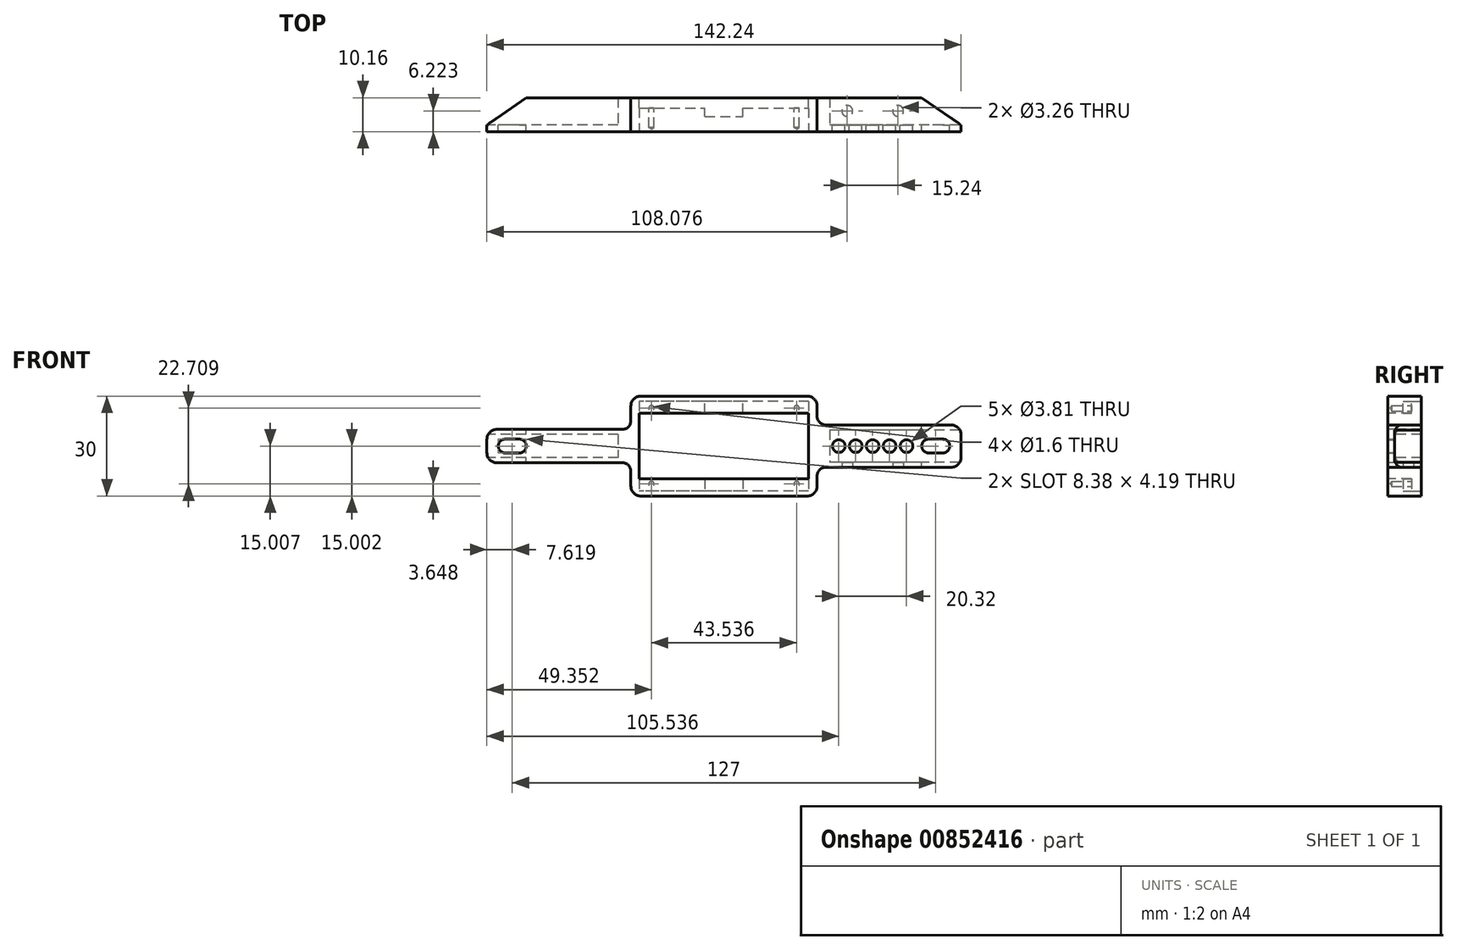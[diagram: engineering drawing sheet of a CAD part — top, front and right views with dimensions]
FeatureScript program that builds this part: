
annotation { "Feature Type Name" : "Feature", "Feature Type Description" : "" }
export const myFeature = defineFeature(function(context is Context, id is Id, definition is map)
    precondition{}
    {
        {
            var Q0;
            Q0=qCreatedBy(makeId("Front.planeOp"),FACE);
            var sketch = newSketch(context, id + "F0", { "sketchPlane" : qUnion([Q0])});
            skLineSegment(sketch, "E0.bottom", {"start": v(21.8, 11.09) * mm, "end": v(72.6, 11.09) * mm});
            skLineSegment(sketch, "E0.top", {"start": v(21.8, -8.62) * mm, "end": v(72.6, -8.62) * mm});
            skLineSegment(sketch, "E0.left", {"start": v(21.8, 11.09) * mm, "end": v(21.8, -8.62) * mm});
            skLineSegment(sketch, "E0.right", {"start": v(72.6, 11.09) * mm, "end": v(72.6, -8.62) * mm});
            skLineSegment(sketch, "E1.bottom", {"start": v(19.27, 16.23) * mm, "end": v(75.15, 16.23) * mm});
            skLineSegment(sketch, "E1.top", {"start": v(19.27, -13.77) * mm, "end": v(75.15, -13.77) * mm});
            skLineSegment(sketch, "E1.left", {"start": v(19.27, 16.23) * mm, "end": v(19.27, -13.77) * mm});
            skLineSegment(sketch, "E1.right", {"start": v(75.15, 16.23) * mm, "end": v(75.15, -13.77) * mm});
            skLineSegment(sketch, "E2.bottom", {"start": v(75.15, 7.58) * mm, "end": v(118.33, 7.58) * mm});
            skLineSegment(sketch, "E2.top", {"start": v(75.15, -5.12) * mm, "end": v(118.33, -5.12) * mm});
            skLineSegment(sketch, "E2.left", {"start": v(75.15, 7.58) * mm, "end": v(75.15, -5.12) * mm});
            skLineSegment(sketch, "E2.right", {"start": v(118.33, 7.58) * mm, "end": v(118.33, -5.12) * mm});
            skLineSegment(sketch, "E3.bottom", {"start": v(19.27, 6.23) * mm, "end": v(-23.91, 6.23) * mm});
            skLineSegment(sketch, "E3.top", {"start": v(19.27, -3.77) * mm, "end": v(-23.91, -3.77) * mm});
            skLineSegment(sketch, "E3.left", {"start": v(19.27, 6.23) * mm, "end": v(19.27, -3.77) * mm});
            skLineSegment(sketch, "E3.right", {"start": v(-23.91, 6.23) * mm, "end": v(-23.91, -3.77) * mm});
            skSolve(sketch);
        }
        {
            var Q0;
            Q0=makeQuery(id+"F0.imprint","IMPRINT",FACE,{"disambiguationData":[TD([[makeQuery(id+"F0.imprint","IMPRINT",EDGE,{"derivedFrom":sQuery(id+"F0.wireOp",EDGE,"E0.bottom")}),1.0]])]});
            var Q1;
            Q1=makeQuery(id+"F0.imprint","IMPRINT",FACE,{"disambiguationData":[TD([[makeQuery(id+"F0.imprint","IMPRINT",EDGE,{"derivedFrom":sQuery(id+"F0.wireOp",EDGE,"E3.bottom")}),1.0]])]});
            var Q2;
            Q2=makeQuery(id+"F0.imprint","IMPRINT",FACE,{"disambiguationData":[TD([[makeQuery(id+"F0.imprint","IMPRINT",EDGE,{"derivedFrom":sQuery(id+"F0.wireOp",EDGE,"E2.bottom")}),-1.0]])]});
            extrude(context, id + "F1", {"entities" : qUnion([Q0, Q1, Q2]), "oppositeDirection" : true, "depth" : 10.16 * mm, "offsetDistance" : 25 * mm});
        }
        {
            var Q0;
            Q0=makeQuery(id+"F1.opExtrude","CAP_FACE",FACE,{"disambiguationData":[OSD([sQuery(id+"F0.wireOp",EDGE,"E0.bottom"),sQuery(id+"F0.wireOp",EDGE,"E0.top"),sQuery(id+"F0.wireOp",EDGE,"E0.left"),sQuery(id+"F0.wireOp",EDGE,"E0.right"),sQuery(id+"F0.wireOp",EDGE,"E1.bottom"),sQuery(id+"F0.wireOp",EDGE,"E1.top"),sQuery(id+"F0.wireOp",EDGE,"E1.left"),sQuery(id+"F0.wireOp",EDGE,"E1.right"),sQuery(id+"F0.wireOp",EDGE,"E2.bottom"),sQuery(id+"F0.wireOp",EDGE,"E2.top"),sQuery(id+"F0.wireOp",EDGE,"E2.right"),sQuery(id+"F0.wireOp",EDGE,"E3.bottom"),sQuery(id+"F0.wireOp",EDGE,"E3.top"),sQuery(id+"F0.wireOp",EDGE,"E3.right")])],"isStart":false});
            var sketch = newSketch(context, id + "F2", { "sketchPlane" : qUnion([Q0])});
            skLineSegment(sketch, "E4.bottom", {"start": v(-72.6, 14.7) * mm, "end": v(-21.8, 14.7) * mm});
            skLineSegment(sketch, "E4.top", {"start": v(-72.6, -12.23) * mm, "end": v(-21.8, -12.23) * mm});
            skLineSegment(sketch, "E4.left", {"start": v(-72.6, 14.7) * mm, "end": v(-72.6, -12.23) * mm});
            skLineSegment(sketch, "E4.right", {"start": v(-21.8, 14.7) * mm, "end": v(-21.8, -12.23) * mm});
            skSolve(sketch);
        }
        {
            var Q0;
            {var subQ0=sQuery(id+"F2.wireOp",EDGE,"E4.top");Q0=makeQuery(id+"F2.imprint","IMPRINT",FACE,{"disambiguationData":[TD([[makeQuery(id+"F2.imprint","IMPRINT",EDGE,{"derivedFrom":subQ0}),1.0]])]});}
            var Q1;
            {var subQ1=makeQuery(id+"F1.opExtrude","CAP_EDGE",EDGE,{"disambiguationData":[OSD([sQuery(id+"F0.wireOp",EDGE,"E0.bottom")])],"isStart":false});Q1=makeQuery(id+"F2.imprint","IMPRINT",FACE,{"disambiguationData":[TD([[makeQuery(id+"F2.imprint","IMPRINT",EDGE,{"derivedFrom":subQ1}),1.0]])]});}
            var Q2;
            {var subQ0=sQuery(id+"F2.wireOp",EDGE,"E4.bottom");Q2=makeQuery(id+"F2.imprint","IMPRINT",FACE,{"disambiguationData":[TD([[makeQuery(id+"F2.imprint","IMPRINT",EDGE,{"derivedFrom":subQ0}),-1.0]])]});}
            extrude(context, id + "F3", {"entities" : qUnion([Q0, Q1, Q2]), "operationType" : NewBodyOperationType.REMOVE, "oppositeDirection" : true, "depth" : 3.05 * mm, "offsetDistance" : 25 * mm});
        }
        {
            var Q0;
            Q0=makeQuery(id+"F1.opExtrude","CAP_FACE",FACE,{"disambiguationData":[OSD([sQuery(id+"F0.wireOp",EDGE,"E0.bottom"),sQuery(id+"F0.wireOp",EDGE,"E0.top"),sQuery(id+"F0.wireOp",EDGE,"E0.left"),sQuery(id+"F0.wireOp",EDGE,"E0.right"),sQuery(id+"F0.wireOp",EDGE,"E1.bottom"),sQuery(id+"F0.wireOp",EDGE,"E1.top"),sQuery(id+"F0.wireOp",EDGE,"E1.left"),sQuery(id+"F0.wireOp",EDGE,"E1.right"),sQuery(id+"F0.wireOp",EDGE,"E2.bottom"),sQuery(id+"F0.wireOp",EDGE,"E2.top"),sQuery(id+"F0.wireOp",EDGE,"E2.right"),sQuery(id+"F0.wireOp",EDGE,"E3.bottom"),sQuery(id+"F0.wireOp",EDGE,"E3.top"),sQuery(id+"F0.wireOp",EDGE,"E3.right")])],"isStart":false});
            var sketch = newSketch(context, id + "F4", { "sketchPlane" : qUnion([Q0])});
            skLineSegment(sketch, "E5.bottom", {"start": v(-118.33, 6.06) * mm, "end": v(-70.07, 6.06) * mm});
            skLineSegment(sketch, "E5.top", {"start": v(-118.33, -3.6) * mm, "end": v(-70.07, -3.6) * mm});
            skLineSegment(sketch, "E5.left", {"start": v(-118.33, 6.06) * mm, "end": v(-118.33, -3.6) * mm});
            skLineSegment(sketch, "E5.right", {"start": v(-70.07, 6.06) * mm, "end": v(-70.07, -3.6) * mm});
            skLineSegment(sketch, "E6.bottom", {"start": v(-24.35, -2.24) * mm, "end": v(36.61, -2.24) * mm});
            skLineSegment(sketch, "E6.top", {"start": v(-24.35, 4.7) * mm, "end": v(36.61, 4.7) * mm});
            skLineSegment(sketch, "E6.left", {"start": v(-24.35, -2.24) * mm, "end": v(-24.35, 4.7) * mm});
            skLineSegment(sketch, "E6.right", {"start": v(36.61, -2.24) * mm, "end": v(36.61, 4.7) * mm});
            skSolve(sketch);
        }
        {
            var Q0;
            Q0=makeQuery(id+"F4.imprint","IMPRINT",FACE,{"disambiguationData":[TD([[makeQuery(id+"F4.imprint","IMPRINT",EDGE,{"derivedFrom":sQuery(id+"F4.wireOp",EDGE,"E5.bottom")}),-1.0]])]});
            var Q1;
            Q1=makeQuery(id+"F4.imprint","IMPRINT",FACE,{"disambiguationData":[TD([[makeQuery(id+"F4.imprint","IMPRINT",EDGE,{"derivedFrom":sQuery(id+"F4.wireOp",EDGE,"E6.bottom")}),1.0]])]});
            extrude(context, id + "F5", {"entities" : qUnion([Q0, Q1]), "operationType" : NewBodyOperationType.REMOVE, "oppositeDirection" : true, "depth" : 8.13 * mm, "offsetDistance" : 25 * mm});
        }
        {
            var Q0;
            Q0=makeQuery(id+"F1.opExtrude","SWEPT_FACE",FACE,{"disambiguationData":[OSD([sQuery(id+"F0.wireOp",EDGE,"E2.bottom")])]});
            var sketch = newSketch(context, id + "F6", { "sketchPlane" : qUnion([Q0])});
            skLineSegment(sketch, "E7", {"start": v(106.52, 10.16) * mm, "end": v(118.33, 2.03) * mm});
            skLineSegment(sketch, "E8", {"start": v(118.33, 2.03) * mm, "end": v(118.33, 0) * mm});
            skLineSegment(sketch, "E9", {"start": v(118.33, 0) * mm, "end": v(106.52, 0) * mm});
            skLineSegment(sketch, "E10", {"start": v(106.52, 0) * mm, "end": v(106.52, 10.16) * mm});
            skSolve(sketch);
        }
        {
            var Q0;
            Q0=makeQuery(id+"F1.opExtrude","SWEPT_FACE",FACE,{"disambiguationData":[OSD([sQuery(id+"F0.wireOp",EDGE,"E3.bottom")])]});
            var sketch = newSketch(context, id + "F7", { "sketchPlane" : qUnion([Q0])});
            skLineSegment(sketch, "E11", {"start": v(-23.91, 2.03) * mm, "end": v(-12.1, 10.16) * mm});
            skLineSegment(sketch, "E12", {"start": v(-12.1, 10.16) * mm, "end": v(-12.1, 0) * mm});
            skLineSegment(sketch, "E13", {"start": v(-12.1, 0) * mm, "end": v(-23.91, 0) * mm});
            skLineSegment(sketch, "E14", {"start": v(-23.91, 0) * mm, "end": v(-23.91, 2.03) * mm});
            skSolve(sketch);
        }
        {
            var Q0;
            {var subQ0=sQuery(id+"F7.wireOp",EDGE,"E11");Q0=makeQuery(id+"F7.imprint","IMPRINT",FACE,{"disambiguationData":[TD([[makeQuery(id+"F7.imprint","IMPRINT",EDGE,{"derivedFrom":subQ0}),1.0]])]});}
            var Q1;
            {var subQ0=sQuery(id+"F6.wireOp",EDGE,"E7");Q1=makeQuery(id+"F6.imprint","IMPRINT",FACE,{"disambiguationData":[TD([[makeQuery(id+"F6.imprint","IMPRINT",EDGE,{"derivedFrom":subQ0}),1.0]])]});}
            extrude(context, id + "F8", {"entities" : qUnion([Q0, Q1]), "operationType" : NewBodyOperationType.REMOVE, "oppositeDirection" : true, "depth" : 25 * mm, "offsetDistance" : 25 * mm});
        }
        {
            var Q0;
            Q0=makeQuery(id+"F5.boolean.opBoolean","COPY",FACE,{"derivedFrom":makeQuery(id+"F5.opExtrude","CAP_FACE",FACE,{"disambiguationData":[OSD([sQuery(id+"F4.wireOp",EDGE,"E5.bottom"),sQuery(id+"F4.wireOp",EDGE,"E5.top"),sQuery(id+"F4.wireOp",EDGE,"E5.left"),sQuery(id+"F4.wireOp",EDGE,"E5.right")])],"isStart":false})});
            var sketch = newSketch(context, id + "F9", { "sketchPlane" : qUnion([Q0])});
            skArc(sketch, "E15", {"start": v(14.2, 3.33) * mm, "mid": v(12.1, 1.24) * mm, "end": v(14.2, -0.86) * mm});
            skArc(sketch, "E16", {"start": v(18.39, -0.86) * mm, "mid": v(20.48, 1.24) * mm, "end": v(18.39, 3.33) * mm});
            skArc(sketch, "E17", {"start": v(-108.61, -0.86) * mm, "mid": v(-106.52, 1.24) * mm, "end": v(-108.61, 3.33) * mm});
            skArc(sketch, "E18", {"start": v(-112.8, 3.33) * mm, "mid": v(-114.9, 1.24) * mm, "end": v(-112.8, -0.86) * mm});
            skLineSegment(sketch, "E19", {"start": v(14.2, 3.33) * mm, "end": v(18.39, 3.33) * mm});
            skLineSegment(sketch, "E20", {"start": v(14.2, -0.86) * mm, "end": v(18.39, -0.86) * mm});
            skLineSegment(sketch, "E21", {"start": v(-112.8, 3.33) * mm, "end": v(-108.61, 3.33) * mm});
            skLineSegment(sketch, "E22", {"start": v(-108.61, -0.86) * mm, "end": v(-112.8, -0.86) * mm});
            skLineSegment(sketch, "E23", {"start": v(18.39, 1.24) * mm, "end": v(14.2, 1.24) * mm});
            skLineSegment(sketch, "E24", {"start": v(-108.61, 1.24) * mm, "end": v(-112.8, 1.24) * mm});
            skPoint(sketch, "E25", {"position": v(-110.7, 1.24) * mm});
            skPoint(sketch, "E26", {"position": v(16.3, 1.24) * mm});
            skLineSegment(sketch, "E27", {"start": v(-72.6, -8.62) * mm, "end": v(-21.8, -8.62) * mm});
            skPoint(sketch, "E28", {"position": v(-47.2, -8.62) * mm});
            skSolve(sketch);
        }
        {
            var Q0;
            Q0=makeQuery(id+"F1.opExtrude","SWEPT_EDGE",EDGE,{"disambiguationData":[OSD([sQuery(id+"F0.wireOp",EDGE,"E1.top"),sQuery(id+"F0.wireOp",EDGE,"E1.right")])]});
            var Q1;
            Q1=makeQuery(id+"F1.opExtrude","SWEPT_EDGE",EDGE,{"disambiguationData":[OSD([sQuery(id+"F0.wireOp",EDGE,"E1.top"),sQuery(id+"F0.wireOp",EDGE,"E1.left")])]});
            var Q2;
            Q2=makeQuery(id+"F1.opExtrude","SWEPT_EDGE",EDGE,{"disambiguationData":[OSD([sQuery(id+"F0.wireOp",EDGE,"E1.bottom"),sQuery(id+"F0.wireOp",EDGE,"E1.left")])]});
            var Q3;
            Q3=makeQuery(id+"F1.opExtrude","SWEPT_EDGE",EDGE,{"disambiguationData":[OSD([sQuery(id+"F0.wireOp",EDGE,"E1.bottom"),sQuery(id+"F0.wireOp",EDGE,"E1.right")])]});
            var Q4;
            Q4=makeQuery(id+"F1.opExtrude","SWEPT_EDGE",EDGE,{"disambiguationData":[OSD([sQuery(id+"F0.wireOp",EDGE,"E3.top"),sQuery(id+"F0.wireOp",EDGE,"E3.right")])]});
            var Q5;
            Q5=makeQuery(id+"F1.opExtrude","SWEPT_EDGE",EDGE,{"disambiguationData":[OSD([sQuery(id+"F0.wireOp",EDGE,"E3.bottom"),sQuery(id+"F0.wireOp",EDGE,"E3.right")])]});
            var Q6;
            Q6=makeQuery(id+"F1.opExtrude","SWEPT_EDGE",EDGE,{"disambiguationData":[OSD([sQuery(id+"F0.wireOp",EDGE,"E2.top"),sQuery(id+"F0.wireOp",EDGE,"E2.right")])]});
            var Q7;
            Q7=makeQuery(id+"F1.opExtrude","SWEPT_EDGE",EDGE,{"disambiguationData":[OSD([sQuery(id+"F0.wireOp",EDGE,"E2.bottom"),sQuery(id+"F0.wireOp",EDGE,"E2.right")])]});
            fillet(context, id + "F10", {"entities" : qUnion([Q0, Q1, Q2, Q3, Q4, Q5, Q6, Q7]), "radius" : 3 * mm, "tangentPropagation" : true, "allowEdgeOverflow" : false});
        }
        {
            var Q0;
            {var subQ0=sQuery(id+"F2.wireOp",EDGE,"E4.top");var subQ1=sQuery(id+"F2.wireOp",EDGE,"E4.left");var subQ2=sQuery(id+"F2.wireOp",EDGE,"E4.right");Q0=makeQuery(id+"F3.boolean.opBoolean","COPY",FACE,{"disambiguationData":[TD([makeQuery(id+"F1.opExtrude","SWEPT_FACE",FACE,{"disambiguationData":[OSD([sQuery(id+"F0.wireOp",EDGE,"E0.top")])]})])],"derivedFrom":makeQuery(id+"F3.opExtrude","CAP_FACE",FACE,{"disambiguationData":[OSD([sQuery(id+"F2.wireOp",EDGE,"E4.bottom"),subQ0,subQ1,subQ2])],"isStart":false})});}
            var sketch = newSketch(context, id + "F11", { "sketchPlane" : qUnion([Q0])});
            skPoint(sketch, "E29", {"position": v(-68.98, 12.59) * mm});
            skPoint(sketch, "E30", {"position": v(-25.44, 12.59) * mm});
            skPoint(sketch, "E31", {"position": v(-25.44, -10.12) * mm});
            skPoint(sketch, "E32", {"position": v(-68.98, -10.12) * mm});
            skSolve(sketch);
        }
        {
            var Q0;
            Q0=sQuery(id+"F11.wireOp",VERTEX,"E29");
            var Q1;
            Q1=sQuery(id+"F11.wireOp",VERTEX,"E30");
            var Q2;
            Q2=sQuery(id+"F11.wireOp",VERTEX,"E31");
            var Q3;
            Q3=sQuery(id+"F11.wireOp",VERTEX,"E32");
            var Q4;
            Q4=makeQuery(id+"F1.opExtrude","SWEPT_BODY",BODY,{"disambiguationData":[OSD([sQuery(id+"F0.wireOp",EDGE,"E0.bottom"),sQuery(id+"F0.wireOp",EDGE,"E0.top"),sQuery(id+"F0.wireOp",EDGE,"E0.left"),sQuery(id+"F0.wireOp",EDGE,"E0.right"),sQuery(id+"F0.wireOp",EDGE,"E1.bottom"),sQuery(id+"F0.wireOp",EDGE,"E1.top"),sQuery(id+"F0.wireOp",EDGE,"E1.left"),sQuery(id+"F0.wireOp",EDGE,"E1.right"),sQuery(id+"F0.wireOp",EDGE,"E2.bottom"),sQuery(id+"F0.wireOp",EDGE,"E2.top"),sQuery(id+"F0.wireOp",EDGE,"E2.right"),sQuery(id+"F0.wireOp",EDGE,"E3.bottom"),sQuery(id+"F0.wireOp",EDGE,"E3.top"),sQuery(id+"F0.wireOp",EDGE,"E3.right")])]});
            hole(context, id + "F12", {"style" : HoleStyle.SIMPLE, "endStyle" : HoleEndStyle.BLIND, "holeDiameter" : 1.6 * mm, "majorDiameter" : 3 * mm, "holeDepth" : 5.84 * mm, "isTappedThrough" : true, "tappedDepth" : 3.18 * mm, "tapClearance" : 3, "startFromSketch" : true, "locations" : qUnion([Q0, Q1, Q2, Q3]), "scope" : qUnion([Q4])});
        }
        {
            var Q0;
            {var subQ0=sQuery(id+"F2.wireOp",EDGE,"E4.bottom");var subQ1=sQuery(id+"F2.wireOp",EDGE,"E4.left");var subQ2=sQuery(id+"F2.wireOp",EDGE,"E4.right");Q0=makeQuery(id+"F3.boolean.opBoolean","COPY",FACE,{"disambiguationData":[TD([makeQuery(id+"F1.opExtrude","SWEPT_FACE",FACE,{"disambiguationData":[OSD([sQuery(id+"F0.wireOp",EDGE,"E0.bottom")])]})])],"derivedFrom":makeQuery(id+"F3.opExtrude","CAP_FACE",FACE,{"disambiguationData":[OSD([subQ0,sQuery(id+"F2.wireOp",EDGE,"E4.top"),subQ1,subQ2])],"isStart":false})});}
            var sketch = newSketch(context, id + "F13", { "sketchPlane" : qUnion([Q0])});
            skLineSegment(sketch, "E33.bottom", {"start": v(-47.2, 11.09) * mm, "end": v(-52.92, 11.09) * mm});
            skLineSegment(sketch, "E33.top", {"start": v(-47.2, 14.7) * mm, "end": v(-52.92, 14.7) * mm});
            skLineSegment(sketch, "E33.left", {"start": v(-47.2, 11.09) * mm, "end": v(-47.2, 14.7) * mm});
            skLineSegment(sketch, "E33.right", {"start": v(-52.92, 11.09) * mm, "end": v(-52.92, 14.7) * mm});
            skLineSegment(sketch, "E34.bottom", {"start": v(-47.2, 11.09) * mm, "end": v(-41.5, 11.09) * mm});
            skLineSegment(sketch, "E34.top", {"start": v(-47.2, 14.7) * mm, "end": v(-41.5, 14.7) * mm});
            skLineSegment(sketch, "E34.right", {"start": v(-41.5, 11.09) * mm, "end": v(-41.5, 14.7) * mm});
            skSolve(sketch);
        }
        {
            var Q0;
            Q0=makeQuery(id+"F13.imprint","IMPRINT",FACE,{"disambiguationData":[TD([[makeQuery(id+"F13.imprint","IMPRINT",EDGE,{"derivedFrom":sQuery(id+"F13.wireOp",EDGE,"E33.bottom")}),-1.0]])]});
            var Q1;
            Q1=makeQuery(id+"F13.imprint","IMPRINT",FACE,{"disambiguationData":[TD([[makeQuery(id+"F13.imprint","IMPRINT",EDGE,{"derivedFrom":sQuery(id+"F13.wireOp",EDGE,"E34.bottom")}),-1.0]])]});
            extrude(context, id + "F14", {"entities" : qUnion([Q0, Q1]), "operationType" : NewBodyOperationType.REMOVE, "oppositeDirection" : true, "depth" : 2.54 * mm, "offsetDistance" : 25.4 * mm});
        }
        {
            var Q0;
            {var subQ0=sQuery(id+"F2.wireOp",EDGE,"E4.top");var subQ1=sQuery(id+"F2.wireOp",EDGE,"E4.left");var subQ2=sQuery(id+"F2.wireOp",EDGE,"E4.right");Q0=makeQuery(id+"F3.boolean.opBoolean","COPY",FACE,{"disambiguationData":[TD([makeQuery(id+"F1.opExtrude","SWEPT_FACE",FACE,{"disambiguationData":[OSD([sQuery(id+"F0.wireOp",EDGE,"E0.top")])]})])],"derivedFrom":makeQuery(id+"F3.opExtrude","CAP_FACE",FACE,{"disambiguationData":[OSD([sQuery(id+"F2.wireOp",EDGE,"E4.bottom"),subQ0,subQ1,subQ2])],"isStart":false})});}
            var sketch = newSketch(context, id + "F15", { "sketchPlane" : qUnion([Q0])});
            skLineSegment(sketch, "E35.bottom", {"start": v(-47.2, -8.62) * mm, "end": v(-52.92, -8.62) * mm});
            skLineSegment(sketch, "E35.top", {"start": v(-47.2, -12.23) * mm, "end": v(-52.92, -12.23) * mm});
            skLineSegment(sketch, "E35.left", {"start": v(-47.2, -8.62) * mm, "end": v(-47.2, -12.23) * mm});
            skLineSegment(sketch, "E35.right", {"start": v(-52.92, -8.62) * mm, "end": v(-52.92, -12.23) * mm});
            skLineSegment(sketch, "E36.bottom", {"start": v(-47.2, -8.62) * mm, "end": v(-41.5, -8.62) * mm});
            skLineSegment(sketch, "E36.top", {"start": v(-47.2, -12.23) * mm, "end": v(-41.5, -12.23) * mm});
            skLineSegment(sketch, "E36.right", {"start": v(-41.5, -8.62) * mm, "end": v(-41.5, -12.23) * mm});
            skSolve(sketch);
        }
        {
            var Q0;
            Q0=makeQuery(id+"F15.imprint","IMPRINT",FACE,{"disambiguationData":[TD([[makeQuery(id+"F15.imprint","IMPRINT",EDGE,{"derivedFrom":sQuery(id+"F15.wireOp",EDGE,"E35.bottom")}),1.0]])]});
            var Q1;
            Q1=makeQuery(id+"F15.imprint","IMPRINT",FACE,{"disambiguationData":[TD([[makeQuery(id+"F15.imprint","IMPRINT",EDGE,{"derivedFrom":sQuery(id+"F15.wireOp",EDGE,"E36.bottom")}),1.0]])]});
            extrude(context, id + "F16", {"entities" : qUnion([Q0, Q1]), "operationType" : NewBodyOperationType.REMOVE, "oppositeDirection" : true, "depth" : 2.54 * mm, "offsetDistance" : 25.4 * mm});
        }
        {
            var Q0;
            Q0=makeQuery(id+"F9.imprint","IMPRINT",FACE,{"disambiguationData":[TD([[makeQuery(id+"F9.imprint","IMPRINT",EDGE,{"derivedFrom":sQuery(id+"F9.wireOp",EDGE,"E17")}),1.0]])]});
            var Q1;
            {var subQ0=sQuery(id+"F9.wireOp",EDGE,"E15");Q1=makeQuery(id+"F9.imprint","IMPRINT",FACE,{"disambiguationData":[TD([[makeQuery(id+"F9.imprint","IMPRINT",EDGE,{"derivedFrom":subQ0}),1.0]])]});}
            extrude(context, id + "F17", {"entities" : qUnion([Q0, Q1]), "operationType" : NewBodyOperationType.REMOVE, "oppositeDirection" : true, "depth" : 25.4 * mm, "offsetDistance" : 25.4 * mm});
        }
        {
            var Q0;
            Q0=makeQuery(id+"F1.opExtrude","SWEPT_EDGE",EDGE,{"disambiguationData":[OSD([sQuery(id+"F0.wireOp",EDGE,"E1.right"),sQuery(id+"F0.wireOp",EDGE,"E2.bottom"),sQuery(id+"F0.wireOp",EDGE,"E2.left")])]});
            var Q1;
            Q1=makeQuery(id+"F1.opExtrude","SWEPT_EDGE",EDGE,{"disambiguationData":[OSD([sQuery(id+"F0.wireOp",EDGE,"E1.right"),sQuery(id+"F0.wireOp",EDGE,"E2.top"),sQuery(id+"F0.wireOp",EDGE,"E2.left")])]});
            var Q2;
            Q2=makeQuery(id+"F1.opExtrude","SWEPT_EDGE",EDGE,{"disambiguationData":[OSD([sQuery(id+"F0.wireOp",EDGE,"E1.left"),sQuery(id+"F0.wireOp",EDGE,"E3.bottom"),sQuery(id+"F0.wireOp",EDGE,"E3.left")])]});
            var Q3;
            Q3=makeQuery(id+"F1.opExtrude","SWEPT_EDGE",EDGE,{"disambiguationData":[OSD([sQuery(id+"F0.wireOp",EDGE,"E1.left"),sQuery(id+"F0.wireOp",EDGE,"E3.top"),sQuery(id+"F0.wireOp",EDGE,"E3.left")])]});
            var Q4;
            Q4=makeQuery(id+"FJ1hREFEKTw6oiv_1.boolean.opBoolean","COPY",EDGE,{"derivedFrom":makeQuery(id+"FJ1hREFEKTw6oiv_1.opExtrude","SWEPT_EDGE",EDGE,{"disambiguationData":[OSD([sQuery(id+"FbFH97T3WgE5ZJY_1.wireOp",EDGE,"Wi6u83F7-kWvT-Vw4W-9EHg-jvR4nR4GsFJO.top"),sQuery(id+"FbFH97T3WgE5ZJY_1.wireOp",EDGE,"Wi6u83F7-kWvT-Vw4W-9EHg-jvR4nR4GsFJO.left")])]})});
            var Q5;
            Q5=makeQuery(id+"FJ1hREFEKTw6oiv_1.boolean.opBoolean","COPY",EDGE,{"derivedFrom":makeQuery(id+"FJ1hREFEKTw6oiv_1.opExtrude","SWEPT_EDGE",EDGE,{"disambiguationData":[OSD([sQuery(id+"FbFH97T3WgE5ZJY_1.wireOp",EDGE,"Wi6u83F7-kWvT-Vw4W-9EHg-jvR4nR4GsFJO.bottom"),sQuery(id+"FbFH97T3WgE5ZJY_1.wireOp",EDGE,"Wi6u83F7-kWvT-Vw4W-9EHg-jvR4nR4GsFJO.left")])]})});
            var Q6;
            Q6=makeQuery(id+"FJ1hREFEKTw6oiv_1.boolean.opBoolean","COPY",EDGE,{"derivedFrom":makeQuery(id+"FJ1hREFEKTw6oiv_1.opExtrude","SWEPT_EDGE",EDGE,{"disambiguationData":[OSD([sQuery(id+"FbFH97T3WgE5ZJY_1.wireOp",EDGE,"Mb6S61IP-998h-fMWc-2Jxv-Ha52hazkjscY.bottom"),sQuery(id+"FbFH97T3WgE5ZJY_1.wireOp",EDGE,"Mb6S61IP-998h-fMWc-2Jxv-Ha52hazkjscY.left")])]})});
            var Q7;
            Q7=makeQuery(id+"FJ1hREFEKTw6oiv_1.boolean.opBoolean","COPY",EDGE,{"derivedFrom":makeQuery(id+"FJ1hREFEKTw6oiv_1.opExtrude","SWEPT_EDGE",EDGE,{"disambiguationData":[OSD([sQuery(id+"FbFH97T3WgE5ZJY_1.wireOp",EDGE,"Mb6S61IP-998h-fMWc-2Jxv-Ha52hazkjscY.top"),sQuery(id+"FbFH97T3WgE5ZJY_1.wireOp",EDGE,"Mb6S61IP-998h-fMWc-2Jxv-Ha52hazkjscY.left")])]})});
            fillet(context, id + "F18", {"entities" : qUnion([Q0, Q1, Q2, Q3, Q4, Q5, Q6, Q7]), "radius" : 2.54 * mm, "tangentPropagation" : true, "allowEdgeOverflow" : false});
        }
        {
            var Q0;
            Q0=makeQuery(id+"F5.boolean.opBoolean","COPY",FACE,{"derivedFrom":makeQuery(id+"F5.opExtrude","CAP_FACE",FACE,{"disambiguationData":[OSD([sQuery(id+"F4.wireOp",EDGE,"E5.bottom"),sQuery(id+"F4.wireOp",EDGE,"E5.top"),sQuery(id+"F4.wireOp",EDGE,"E5.left"),sQuery(id+"F4.wireOp",EDGE,"E5.right")])],"isStart":false})});
            var sketch = newSketch(context, id + "F19", { "sketchPlane" : qUnion([Q0])});
            skPoint(sketch, "E37", {"position": v(-81.63, 1.23) * mm});
            skPoint(sketch, "E38", {"position": v(-86.7, 1.23) * mm});
            skPoint(sketch, "E39", {"position": v(-91.79, 1.23) * mm});
            skPoint(sketch, "E40", {"position": v(-101.95, 1.23) * mm});
            skPoint(sketch, "E41", {"position": v(-96.87, 1.23) * mm});
            skLineSegment(sketch, "E42", {"start": v(-81.63, 1.23) * mm, "end": v(-86.7, 1.23) * mm});
            skPoint(sketch, "E43", {"position": v(-84.17, 1.23) * mm});
            skSolve(sketch);
        }
        {
            var Q0;
            Q0=sQuery(id+"F19.wireOp",VERTEX,"E40");
            var Q1;
            Q1=sQuery(id+"F19.wireOp",VERTEX,"E39");
            var Q2;
            Q2=sQuery(id+"F19.wireOp",VERTEX,"E37");
            var Q3;
            Q3=sQuery(id+"F19.wireOp",VERTEX,"E38");
            var Q4;
            Q4=sQuery(id+"F19.wireOp",VERTEX,"E41");
            var Q5;
            Q5=makeQuery(id+"F1.opExtrude","SWEPT_BODY",BODY,{"disambiguationData":[OSD([sQuery(id+"F0.wireOp",EDGE,"E0.bottom"),sQuery(id+"F0.wireOp",EDGE,"E0.top"),sQuery(id+"F0.wireOp",EDGE,"E0.left"),sQuery(id+"F0.wireOp",EDGE,"E0.right"),sQuery(id+"F0.wireOp",EDGE,"E1.bottom"),sQuery(id+"F0.wireOp",EDGE,"E1.top"),sQuery(id+"F0.wireOp",EDGE,"E1.left"),sQuery(id+"F0.wireOp",EDGE,"E1.right"),sQuery(id+"F0.wireOp",EDGE,"E2.bottom"),sQuery(id+"F0.wireOp",EDGE,"E2.top"),sQuery(id+"F0.wireOp",EDGE,"E2.right"),sQuery(id+"F0.wireOp",EDGE,"E3.bottom"),sQuery(id+"F0.wireOp",EDGE,"E3.top"),sQuery(id+"F0.wireOp",EDGE,"E3.right")])]});
            hole(context, id + "F20", {"style" : HoleStyle.SIMPLE, "endStyle" : HoleEndStyle.THROUGH, "holeDiameter" : 3.8 * mm, "majorDiameter" : 6.35 * mm, "isTappedThrough" : true, "tappedDepth" : 3.17 * mm, "tapClearance" : 3, "startFromSketch" : true, "locations" : qUnion([Q0, Q1, Q2, Q3, Q4]), "scope" : qUnion([Q5])});
        }
        {
            var Q0;
            Q0=makeQuery(id+"F5.boolean.opBoolean","COPY",FACE,{"derivedFrom":makeQuery(id+"F5.opExtrude","CAP_FACE",FACE,{"disambiguationData":[OSD([sQuery(id+"F4.wireOp",EDGE,"E5.bottom"),sQuery(id+"F4.wireOp",EDGE,"E5.top"),sQuery(id+"F4.wireOp",EDGE,"E5.left"),sQuery(id+"F4.wireOp",EDGE,"E5.right")])],"isStart":false})});
            var sketch = newSketch(context, id + "F21", { "sketchPlane" : qUnion([Q0])});
            skLineSegment(sketch, "E44.bottom", {"start": v(-72.6, 6.06) * mm, "end": v(-78.96, 6.06) * mm});
            skLineSegment(sketch, "E44.top", {"start": v(-72.6, -3.6) * mm, "end": v(-78.96, -3.6) * mm});
            skLineSegment(sketch, "E44.left", {"start": v(-72.6, 6.06) * mm, "end": v(-72.6, -3.6) * mm});
            skLineSegment(sketch, "E44.right", {"start": v(-78.96, 6.06) * mm, "end": v(-78.96, -3.6) * mm});
            skSolve(sketch);
        }
        {
            var Q0;
            Q0=makeQuery(id+"F5.boolean.opBoolean","COPY",FACE,{"derivedFrom":makeQuery(id+"F5.opExtrude","CAP_FACE",FACE,{"disambiguationData":[OSD([sQuery(id+"F4.wireOp",EDGE,"E6.bottom"),sQuery(id+"F4.wireOp",EDGE,"E6.top"),sQuery(id+"F4.wireOp",EDGE,"E6.left"),sQuery(id+"F4.wireOp",EDGE,"E6.right")])],"isStart":false})});
            var sketch = newSketch(context, id + "F22", { "sketchPlane" : qUnion([Q0])});
            skLineSegment(sketch, "E45.bottom", {"start": v(-21.8, 4.7) * mm, "end": v(-15.46, 4.7) * mm});
            skLineSegment(sketch, "E45.top", {"start": v(-21.8, -2.24) * mm, "end": v(-15.46, -2.24) * mm});
            skLineSegment(sketch, "E45.left", {"start": v(-21.8, 4.7) * mm, "end": v(-21.8, -2.24) * mm});
            skLineSegment(sketch, "E45.right", {"start": v(-15.46, 4.7) * mm, "end": v(-15.46, -2.24) * mm});
            skSolve(sketch);
        }
        {
            var Q0;
            Q0=makeQuery(id+"F21.imprint","IMPRINT",FACE,{"disambiguationData":[TD([[makeQuery(id+"F21.imprint","IMPRINT",EDGE,{"derivedFrom":sQuery(id+"F21.wireOp",EDGE,"E44.bottom")}),-1.0]])]});
            var Q1;
            Q1=makeQuery(id+"F22.imprint","IMPRINT",FACE,{"disambiguationData":[TD([[makeQuery(id+"F22.imprint","IMPRINT",EDGE,{"derivedFrom":sQuery(id+"F22.wireOp",EDGE,"E45.bottom")}),-1.0]])]});
            extrude(context, id + "F23", {"entities" : qUnion([Q0, Q1]), "operationType" : NewBodyOperationType.ADD, "depth" : 8.13 * mm, "offsetDistance" : 25.4 * mm});
        }
        {
            var Q0;
            Q0=makeQuery(id+"F1.opExtrude","SWEPT_FACE",FACE,{"disambiguationData":[OSD([sQuery(id+"F0.wireOp",EDGE,"E2.top")])]});
            var sketch = newSketch(context, id + "F24", { "sketchPlane" : qUnion([Q0])});
            skPoint(sketch, "E46", {"position": v(84.17, -6.22) * mm});
            skPoint(sketch, "E47", {"position": v(99.4, -6.22) * mm});
            skSolve(sketch);
        }
        {
            var Q0;
            Q0=sQuery(id+"F24.wireOp",VERTEX,"E46");
            var Q1;
            Q1=sQuery(id+"F24.wireOp",VERTEX,"E47");
            var Q2;
            Q2=makeQuery(id+"F1.opExtrude","SWEPT_BODY",BODY,{"disambiguationData":[OSD([sQuery(id+"F0.wireOp",EDGE,"E0.bottom"),sQuery(id+"F0.wireOp",EDGE,"E0.top"),sQuery(id+"F0.wireOp",EDGE,"E0.left"),sQuery(id+"F0.wireOp",EDGE,"E0.right"),sQuery(id+"F0.wireOp",EDGE,"E1.bottom"),sQuery(id+"F0.wireOp",EDGE,"E1.top"),sQuery(id+"F0.wireOp",EDGE,"E1.left"),sQuery(id+"F0.wireOp",EDGE,"E1.right"),sQuery(id+"F0.wireOp",EDGE,"E2.bottom"),sQuery(id+"F0.wireOp",EDGE,"E2.top"),sQuery(id+"F0.wireOp",EDGE,"E2.right"),sQuery(id+"F0.wireOp",EDGE,"E3.bottom"),sQuery(id+"F0.wireOp",EDGE,"E3.top"),sQuery(id+"F0.wireOp",EDGE,"E3.right")])]});
            hole(context, id + "F25", {"style" : HoleStyle.SIMPLE, "endStyle" : HoleEndStyle.BLIND, "standardTappedOrClearance" : lookupTablePath({ "fit" : "Normal (ASME)", "standard" : "ANSI", "size" : "#4", "type" : "Clearance" }), "standardBlindInLast" : lookupTablePath({ "fit" : "Free", "standard" : "ANSI", "size" : "#4", "type" : "Clearance" }), "holeDiameter" : 3.26 * mm, "majorDiameter" : 2.84 * mm, "holeDepth" : 8.25 * mm, "isTappedThrough" : true, "tappedDepth" : 6.35 * mm, "tapClearance" : 3, "startFromSketch" : true, "locations" : qUnion([Q0, Q1]), "scope" : qUnion([Q2])});
        }
    });
